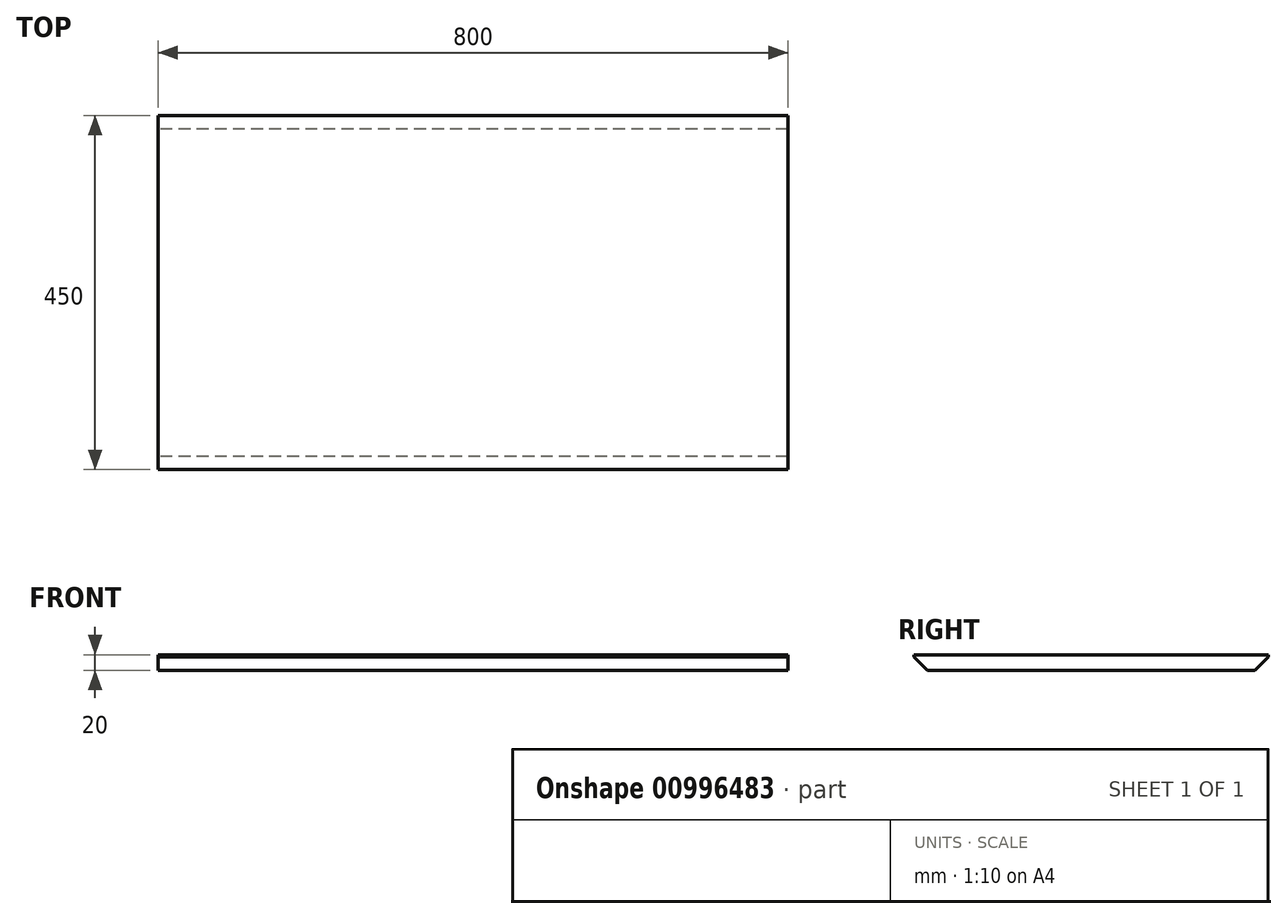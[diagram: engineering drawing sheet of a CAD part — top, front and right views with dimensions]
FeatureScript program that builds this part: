
annotation { "Feature Type Name" : "Feature", "Feature Type Description" : "" }
export const myFeature = defineFeature(function(context is Context, id is Id, definition is map)
    precondition{}
    {
        {
            var Q0;
            Q0=qCreatedBy(makeId("Right.planeOp"),FACE);
            var sketch = newSketch(context, id + "F0", { "sketchPlane" : qUnion([Q0])});
            skLineSegment(sketch, "E0.bottom", {"start": v(225, 10) * mm, "end": v(-225, 10) * mm});
            skLineSegment(sketch, "E0.top", {"start": v(208, -10) * mm, "end": v(-208, -10) * mm});
            skLineSegment(sketch, "E0.left", {"start": v(225, 10) * mm, "end": v(225, 7) * mm});
            skLineSegment(sketch, "E0.right", {"start": v(-225, 10) * mm, "end": v(-225, 7) * mm});
            skPoint(sketch, "E0.middle", {"position": v(0, 0) * mm});
            skLineSegment(sketch, "E1", {"start": v(-225, 7) * mm, "end": v(-208, -10) * mm});
            skPoint(sketch, "E2.orphan", {"position": v(-225, -10) * mm});
            skLineSegment(sketch, "E3", {"start": v(225, 7) * mm, "end": v(208, -10) * mm});
            skPoint(sketch, "E4.orphan", {"position": v(225, -10) * mm});
            skSolve(sketch);
        }
        {
            var Q0;
            Q0=makeQuery(id+"F0.imprint","IMPRINT",FACE,{"disambiguationData":[TD([[makeQuery(id+"F0.imprint","IMPRINT",EDGE,{"derivedFrom":sQuery(id+"F0.wireOp",EDGE,"E0.bottom")}),1.0]])]});
            extrude(context, id + "F1", {"entities" : qUnion([Q0]), "endBound" : BoundingType.SYMMETRIC, "depth" : 800 * mm, "offsetDistance" : 25 * mm});
        }
    });
